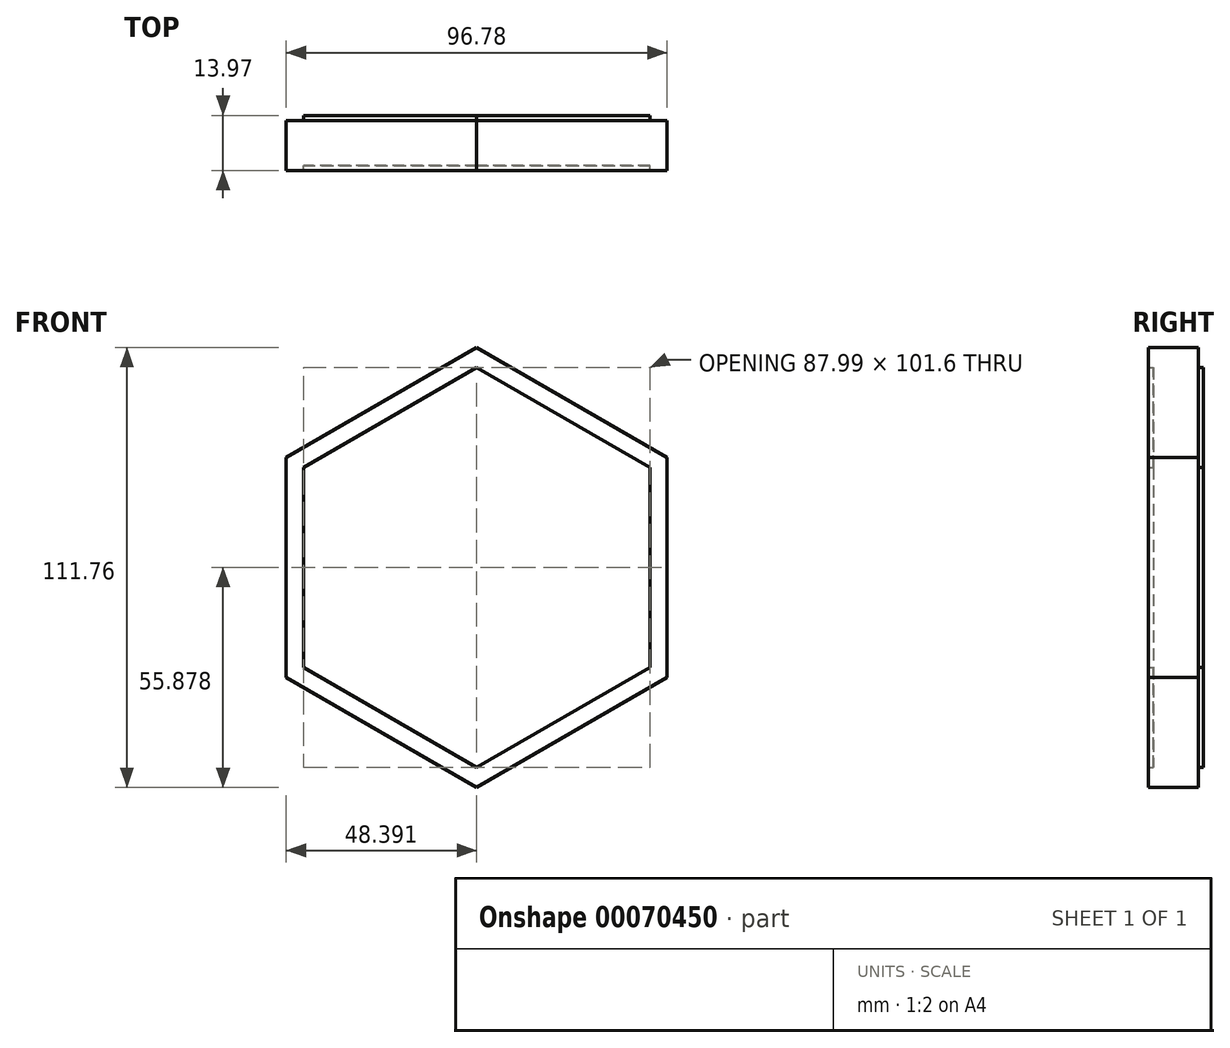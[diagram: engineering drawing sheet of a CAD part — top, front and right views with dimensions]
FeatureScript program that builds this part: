
annotation { "Feature Type Name" : "Feature", "Feature Type Description" : "" }
export const myFeature = defineFeature(function(context is Context, id is Id, definition is map)
    precondition{}
    {
        {
            var Q0;
            Q0=qCreatedBy(makeId("Front.planeOp"),FACE);
            var sketch = newSketch(context, id + "F0", { "sketchPlane" : qUnion([Q0])});
            skLineSegment(sketch, "E0", {"start": v(-44, 25.4) * mm, "end": v(-44, -25.4) * mm});
            skLineSegment(sketch, "E1", {"start": v(-44, 25.4) * mm, "end": v(0, 50.8) * mm});
            skLineSegment(sketch, "E2", {"start": v(0, 50.8) * mm, "end": v(44, 25.4) * mm});
            skLineSegment(sketch, "E3", {"start": v(44, 25.4) * mm, "end": v(44, -25.4) * mm});
            skLineSegment(sketch, "E4", {"start": v(44, -25.4) * mm, "end": v(0, -50.8) * mm});
            skLineSegment(sketch, "E5", {"start": v(0, -50.8) * mm, "end": v(-44, -25.4) * mm});
            skSolve(sketch);
        }
        {
            var Q0;
            Q0=makeQuery(id+"F0.imprint","IMPRINT",FACE,{"disambiguationData":[TD([[makeQuery(id+"F0.imprint","IMPRINT",EDGE,{"derivedFrom":sQuery(id+"F0.wireOp",EDGE,"E0")}),1.0]])]});
            extrude(context, id + "F1", {"entities" : qUnion([Q0]), "depth" : 12.7 * mm});
        }
        {
            var Q0;
            Q0=makeQuery(id+"F1.opExtrude","CAP_FACE",FACE,{"disambiguationData":[OSD([sQuery(id+"F0.wireOp",EDGE,"E0"),sQuery(id+"F0.wireOp",EDGE,"E1"),sQuery(id+"F0.wireOp",EDGE,"E2"),sQuery(id+"F0.wireOp",EDGE,"E3"),sQuery(id+"F0.wireOp",EDGE,"E4"),sQuery(id+"F0.wireOp",EDGE,"E5")])],"isStart":false});
            var sketch = newSketch(context, id + "F2", { "sketchPlane" : qUnion([Q0])});
            skLineSegment(sketch, "E6", {"start": v(0, 55.88) * mm, "end": v(48.4, 27.94) * mm});
            skLineSegment(sketch, "E7", {"start": v(48.4, 27.94) * mm, "end": v(48.4, -27.94) * mm});
            skLineSegment(sketch, "E8", {"start": v(48.4, -27.94) * mm, "end": v(0, -55.88) * mm});
            skLineSegment(sketch, "E9", {"start": v(0, -55.88) * mm, "end": v(-48.4, -27.94) * mm});
            skLineSegment(sketch, "E10", {"start": v(-48.4, -27.94) * mm, "end": v(-48.4, 27.94) * mm});
            skLineSegment(sketch, "E11", {"start": v(-48.4, 27.94) * mm, "end": v(0, 55.88) * mm});
            skLineSegment(sketch, "E12", {"start": v(-44, 25.4) * mm, "end": v(0, 50.8) * mm});
            skLineSegment(sketch, "E13", {"start": v(0, 50.8) * mm, "end": v(44, 25.4) * mm});
            skLineSegment(sketch, "E14", {"start": v(44, 25.4) * mm, "end": v(44, -25.4) * mm});
            skLineSegment(sketch, "E15", {"start": v(44, -25.4) * mm, "end": v(0, -50.8) * mm});
            skLineSegment(sketch, "E16", {"start": v(0, -50.8) * mm, "end": v(-44, -25.4) * mm});
            skLineSegment(sketch, "E17", {"start": v(-44, -25.4) * mm, "end": v(-44, 25.4) * mm});
            skSolve(sketch);
        }
        {
            var Q0;
            Q0=makeQuery(id+"F2.imprint","IMPRINT",FACE,{"disambiguationData":[TD([[makeQuery(id+"F2.imprint","IMPRINT",EDGE,{"derivedFrom":sQuery(id+"F2.wireOp",EDGE,"E6")}),-1.0]])]});
            extrude(context, id + "F3", {"entities" : qUnion([Q0]), "depth" : 1.27 * mm});
        }
        {
            var Q0;
            Q0=makeQuery(id+"F3.opExtrude","CAP_FACE",FACE,{"disambiguationData":[OSD([sQuery(id+"F2.wireOp",EDGE,"E6"),sQuery(id+"F2.wireOp",EDGE,"E7"),sQuery(id+"F2.wireOp",EDGE,"E8"),sQuery(id+"F2.wireOp",EDGE,"E9"),sQuery(id+"F2.wireOp",EDGE,"E10"),sQuery(id+"F2.wireOp",EDGE,"E11"),sQuery(id+"F2.wireOp",EDGE,"E12"),sQuery(id+"F2.wireOp",EDGE,"E13"),sQuery(id+"F2.wireOp",EDGE,"E14"),sQuery(id+"F2.wireOp",EDGE,"E15"),sQuery(id+"F2.wireOp",EDGE,"E16"),sQuery(id+"F2.wireOp",EDGE,"E17")])],"isStart":true});
            extrude(context, id + "F4", {"entities" : qUnion([Q0]), "operationType" : NewBodyOperationType.ADD, "depth" : 11.43 * mm});
        }
    });
